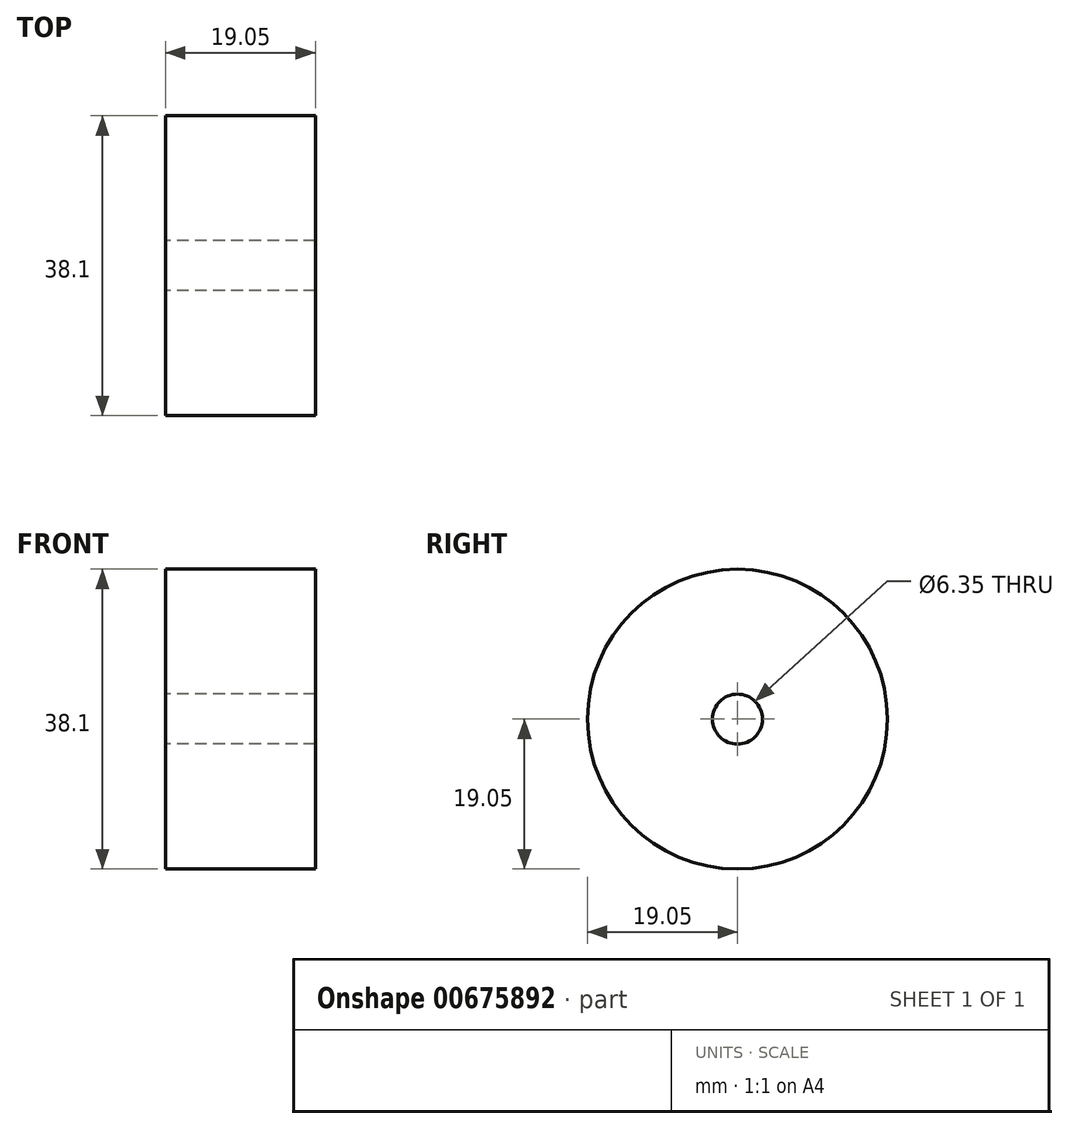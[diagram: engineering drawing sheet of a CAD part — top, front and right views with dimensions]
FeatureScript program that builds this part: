
annotation { "Feature Type Name" : "Feature", "Feature Type Description" : "" }
export const myFeature = defineFeature(function(context is Context, id is Id, definition is map)
    precondition{}
    {
        {
            var Q0;
            Q0=qCreatedBy(makeId("Right.planeOp"),FACE);
            var sketch = newSketch(context, id + "F0", { "sketchPlane" : qUnion([Q0])});
            skCircle(sketch, "E0", {"center": v(0, 0) * mm, "radius": 19.05 * mm});
            skCircle(sketch, "E1", {"center": v(0, 0) * mm, "radius": 3.18 * mm});
            skSolve(sketch);
        }
        {
            var Q0;
            Q0 = qSketchRegion(id + "F0", true);
            extrude(context, id + "F1", {"entities" : qUnion([Q0]), "depth" : 19.05 * mm, "offsetDistance" : 25.4 * mm});
        }
    });
